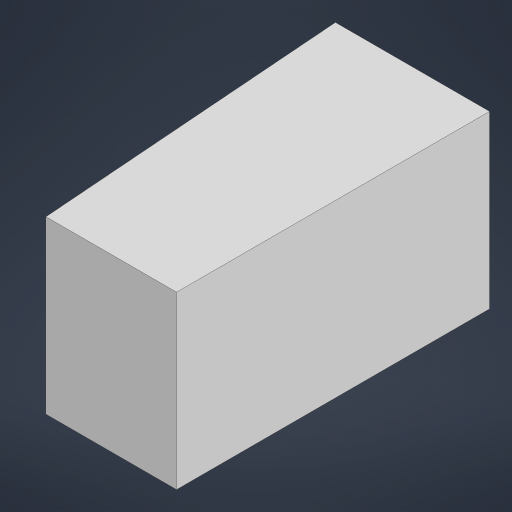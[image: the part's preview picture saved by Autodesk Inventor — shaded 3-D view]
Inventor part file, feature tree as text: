
AUTODESK INVENTOR PART (.ipt)
format: ipt  version: 2023 (Build 270158000, 158)  size: 127,488 bytes
history: native  units: in
note: dims shown in document units (in); Inventor stores cm internally (conversion verified against a paired STEP export)
features: extrude x1, sketch x1
ambient origin geometry x8: Origin, YZ Plane, XZ Plane, XY Plane, X Axis, Y Axis, Z Axis, Center Point
bodies: Solid1 (feature_tree)
feature tree (2):
  extrude  "Extrusion1"  Depth=1.8307in
  sketch  "Sketch1"  dims[d6=0.7638in d7=1.8307in d8=0.9016in d9=1.0in d10=0.0in]
